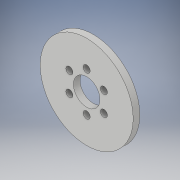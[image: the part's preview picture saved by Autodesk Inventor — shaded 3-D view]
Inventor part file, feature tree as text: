
AUTODESK INVENTOR PART (.ipt)
format: ipt  version: 2019 (Build 230136000, 136)  size: 120,320 bytes
history: native  units: in
note: dims shown in document units (in); Inventor stores cm internally (conversion verified against a paired STEP export)
features: extrude x2, sketch x2
ambient origin geometry x8: Origin, YZ Plane, XZ Plane, XY Plane, X Axis, Y Axis, Z Axis, Center Point
bodies: Solid1 (feature_tree)
feature tree (4):
  extrude  "Extrusion1"  Depth=3.5in
  extrude  "Extrusion2"  Depth=0.25in
  sketch  "Sketch1"  dims[d0=1.0in d1=3.5in]
  sketch  "Sketch2"  dims[d2=0.25in d3=0.0in d4=1.5in d5=0.266in d6=2.3622in d8=360.0deg d10=0.25in d11=0.0in]
